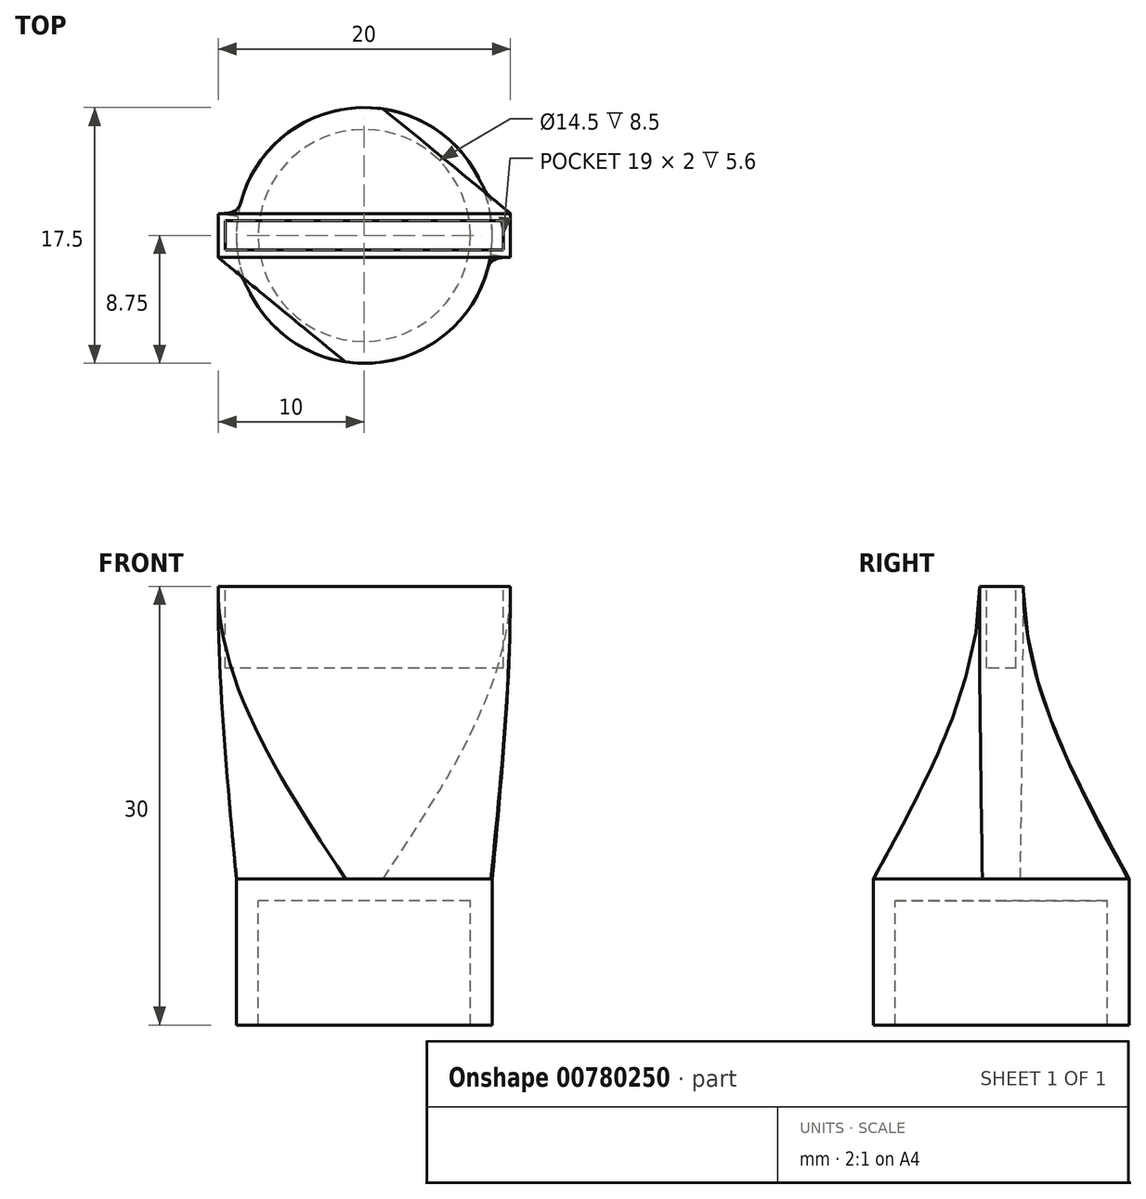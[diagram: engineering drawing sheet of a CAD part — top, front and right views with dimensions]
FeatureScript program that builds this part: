
annotation { "Feature Type Name" : "Feature", "Feature Type Description" : "" }
export const myFeature = defineFeature(function(context is Context, id is Id, definition is map)
    precondition{}
    {
        {
            var Q0;
            Q0=qCreatedBy(makeId("Top.planeOp"),FACE);
            var sketch = newSketch(context, id + "F0", { "sketchPlane" : qUnion([Q0])});
            skCircle(sketch, "E0", {"center": v(0, 0) * mm, "radius": 8.75 * mm});
            skSolve(sketch);
        }
        {
            var Q0;
            Q0=qCreatedBy(makeId("Top.planeOp"),FACE);
            cPlane(context, id + "F1", {"entities" : qUnion([Q0]), "cplaneType" : CPlaneType.OFFSET, "offset" : 20 * mm, "width" : 150 * mm, "height" : 150 * mm});
        }
        {
            var Q0;
            Q0=qCreatedBy(id+"F1.planeOp",FACE);
            var sketch = newSketch(context, id + "F2", { "sketchPlane" : qUnion([Q0])});
            skLineSegment(sketch, "E1.bottom", {"start": v(-10, 1.5) * mm, "end": v(10, 1.5) * mm});
            skLineSegment(sketch, "E1.top", {"start": v(-10, -1.5) * mm, "end": v(10, -1.5) * mm});
            skLineSegment(sketch, "E1.left", {"start": v(-10, 1.5) * mm, "end": v(-10, -1.5) * mm});
            skLineSegment(sketch, "E1.right", {"start": v(10, 1.5) * mm, "end": v(10, -1.5) * mm});
            skSolve(sketch);
        }
        {
            var Q0;
            Q0=makeQuery(id+"F0.imprint","IMPRINT",FACE,{"disambiguationData":[TD([[makeQuery(id+"F0.imprint","IMPRINT",EDGE,{"derivedFrom":sQuery(id+"F0.wireOp",EDGE,"E0")}),1.0]])]});
            var Q1;
            Q1=makeQuery(id+"F2.imprint","IMPRINT",FACE,{"disambiguationData":[TD([[makeQuery(id+"F2.imprint","IMPRINT",EDGE,{"derivedFrom":sQuery(id+"F2.wireOp",EDGE,"E1.bottom")}),-1.0]])]});
            loft(context, id + "F3", {"endCondition" : LoftEndDerivativeType.NORMAL_TO_PROFILE, "endMagnitude" : 1, "sheetProfilesArray" : [{ "sheetProfileEntities" : qUnion([Q0]) }, { "sheetProfileEntities" : qUnion([Q1]) }]});
        }
        {
            var Q0;
            Q0 = qSketchRegion(id + "F0", true);
            extrude(context, id + "F4", {"entities" : qUnion([Q0]), "oppositeDirection" : true, "depth" : 10 * mm, "offsetDistance" : 25 * mm});
        }
        {
            var Q0;
            Q0=makeQuery(id+"F4.opExtrude","CAP_FACE",FACE,{"disambiguationData":[OSD([sQuery(id+"F0.wireOp",EDGE,"E0")])],"isStart":false});
            shell(context, id + "F5", {"entities" : qUnion([Q0]), "thickness" : 1.5 * mm});
        }
        {
            var Q0;
            Q0=makeQuery(id+"F3.opLoft","CAP_FACE",FACE,{"disambiguationData":[OSD([makeQuery(id+"F2.imprint","IMPRINT",FACE,{"disambiguationData":[TD([[makeQuery(id+"F2.imprint","IMPRINT",EDGE,{"derivedFrom":sQuery(id+"F2.wireOp",EDGE,"E1.bottom")}),-1.0]])]})])],"isStart":true});
            var sketch = newSketch(context, id + "F6", { "sketchPlane" : qUnion([Q0])});
            skLineSegment(sketch, "E2.bottom", {"start": v(9.5, 1) * mm, "end": v(-9.5, 1) * mm});
            skLineSegment(sketch, "E2.top", {"start": v(9.5, -1) * mm, "end": v(-9.5, -1) * mm});
            skLineSegment(sketch, "E2.left", {"start": v(9.5, 1) * mm, "end": v(9.5, -1) * mm});
            skLineSegment(sketch, "E2.right", {"start": v(-9.5, 1) * mm, "end": v(-9.5, -1) * mm});
            skSolve(sketch);
        }
        {
            var Q0;
            Q0 = qSketchRegion(id + "F6", true);
            extrude(context, id + "F7", {"entities" : qUnion([Q0]), "operationType" : NewBodyOperationType.REMOVE, "oppositeDirection" : true, "depth" : 5.6 * mm, "offsetDistance" : 25 * mm});
        }
    });
